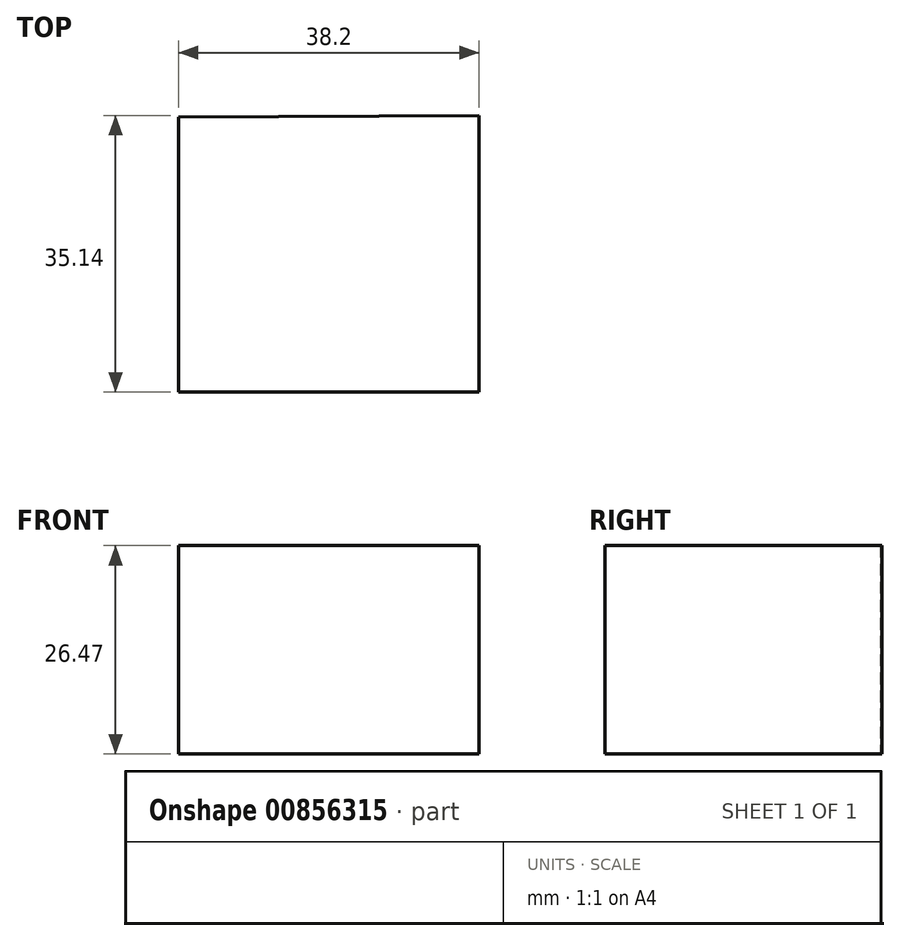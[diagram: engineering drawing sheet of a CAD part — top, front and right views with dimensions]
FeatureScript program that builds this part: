
annotation { "Feature Type Name" : "Feature", "Feature Type Description" : "" }
export const myFeature = defineFeature(function(context is Context, id is Id, definition is map)
    precondition{}
    {
        {
            var Q0;
            Q0=qCreatedBy(makeId("Top.planeOp"),FACE);
            var sketch = newSketch(context, id + "F0", { "sketchPlane" : qUnion([Q0])});
            skLineSegment(sketch, "E0", {"start": v(-21.14, 16.18) * mm, "end": v(-21.14, -18.76) * mm});
            skLineSegment(sketch, "E1", {"start": v(-21.14, -18.76) * mm, "end": v(17.06, -18.76) * mm});
            skLineSegment(sketch, "E2", {"start": v(17.06, -18.76) * mm, "end": v(17.06, 16.38) * mm});
            skLineSegment(sketch, "E3", {"start": v(17.06, 16.38) * mm, "end": v(-21.14, 16.18) * mm});
            skSolve(sketch);
        }
        {
            var Q0;
            Q0 = qSketchRegion(id + "F0", true);
            var Q1;
            Q1=makeQuery(id+"F0.imprint","IMPRINT",FACE,{"disambiguationData":[TD([[makeQuery(id+"F0.imprint","IMPRINT",EDGE,{"derivedFrom":sQuery(id+"F0.wireOp",EDGE,"E0")}),1.0]])]});
            extrude(context, id + "F1", {"entities" : qUnion([Q0, Q1]), "depth" : 26.47 * mm, "offsetDistance" : 25.4 * mm});
        }
    });
